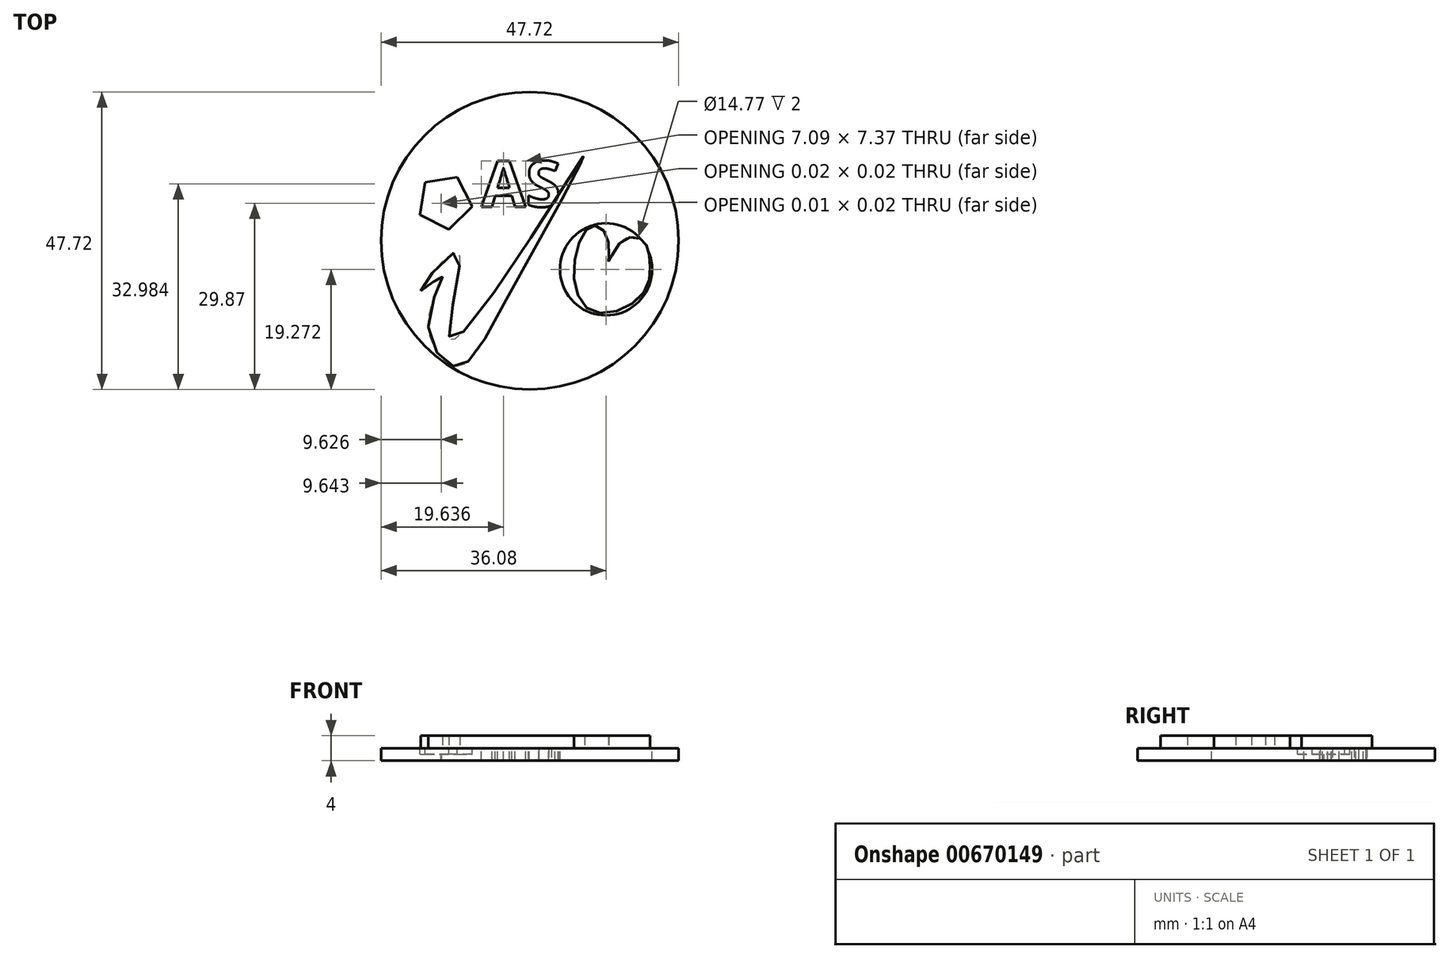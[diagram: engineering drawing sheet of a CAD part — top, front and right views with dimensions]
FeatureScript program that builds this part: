
annotation { "Feature Type Name" : "Feature", "Feature Type Description" : "" }
export const myFeature = defineFeature(function(context is Context, id is Id, definition is map)
    precondition{}
    {
        {
            var Q0;
            Q0=qCreatedBy(makeId("Top.planeOp"),FACE);
            var sketch = newSketch(context, id + "F0", { "sketchPlane" : qUnion([Q0])});
            skCircle(sketch, "E0", {"center": v(0, 0) * mm, "radius": 23.86 * mm});
            skSolve(sketch);
        }
        {
            var Q0;
            Q0=makeQuery(id+"F0.imprint","IMPRINT",FACE,{"disambiguationData":[TD([[makeQuery(id+"F0.imprint","IMPRINT",EDGE,{"derivedFrom":sQuery(id+"F0.wireOp",EDGE,"E0")}),1.0]])]});
            extrude(context, id + "F1", {"entities" : qUnion([Q0]), "oppositeDirection" : true, "depth" : 2 * mm, "offsetDistance" : 25.4 * mm});
        }
        {
            var Q0;
            Q0=makeQuery(id+"F0.imprint","IMPRINT",FACE,{"disambiguationData":[TD([[makeQuery(id+"F0.imprint","IMPRINT",EDGE,{"derivedFrom":sQuery(id+"F0.wireOp",EDGE,"E0")}),1.0]])]});
            var sketch = newSketch(context, id + "F2", { "sketchPlane" : qUnion([Q0])});
            skCircle(sketch, "E1.cCircle", {"center": v(-13.65, 6.19) * mm, "radius": 3.6 * mm, "construction": true});
            skLineSegment(sketch, "E1.0", {"start": v(-9.25, 5.5) * mm, "end": v(-12.96, 1.79) * mm});
            skLineSegment(sketch, "E1.1", {"start": v(-12.96, 1.79) * mm, "end": v(-17.62, 4.17) * mm});
            skLineSegment(sketch, "E1.2", {"start": v(-17.62, 4.17) * mm, "end": v(-16.8, 9.34) * mm});
            skLineSegment(sketch, "E1.3", {"start": v(-16.8, 9.34) * mm, "end": v(-11.63, 10.16) * mm});
            skLineSegment(sketch, "E1.4", {"start": v(-11.63, 10.16) * mm, "end": v(-9.25, 5.5) * mm});
            skPoint(sketch, "E1.0.midPoint", {"position": v(-11.1, 3.64) * mm});
            skSolve(sketch);
        }
        {
            var Q0;
            Q0 = qSketchRegion(id + "F2", true);
            extrude(context, id + "F3", {"entities" : qUnion([Q0]), "operationType" : NewBodyOperationType.REMOVE, "oppositeDirection" : true, "depth" : 1 * mm, "offsetDistance" : 25.4 * mm});
        }
        {
            var Q0;
            Q0=makeQuery(id+"F0.imprint","IMPRINT",FACE,{"disambiguationData":[TD([[makeQuery(id+"F0.imprint","IMPRINT",EDGE,{"derivedFrom":sQuery(id+"F0.wireOp",EDGE,"E0")}),1.0]])]});
            var sketch = newSketch(context, id + "F4", { "sketchPlane" : qUnion([Q0])});
            skCircle(sketch, "E2", {"center": v(12.22, -4.59) * mm, "radius": 7.38 * mm});
            skSolve(sketch);
        }
        {
            var Q0;
            Q0 = qSketchRegion(id + "F4", true);
            extrude(context, id + "F5", {"entities" : qUnion([Q0]), "operationType" : NewBodyOperationType.REMOVE, "oppositeDirection" : true, "depth" : 2 * mm, "offsetDistance" : 25.4 * mm});
        }
        {
            var Q0;
            Q0=makeQuery(id+"F0.imprint","IMPRINT",FACE,{"disambiguationData":[TD([[makeQuery(id+"F0.imprint","IMPRINT",EDGE,{"derivedFrom":sQuery(id+"F0.wireOp",EDGE,"E0")}),1.0]])]});
            var sketch = newSketch(context, id + "F6", { "sketchPlane" : qUnion([Q0])});
            skText(sketch, "E3", { "text": "AS", "fontName": "OpenSans-Italic.ttf"});
            skText(sketch, "E4", { "text": "AS", "fontName": "OpenSans-Bold.ttf"});
            const initialGuessF6  = {"E3": [-0.01424, 0.006, 1, 0, 2e-05], "E4": [-0.00777, 0.00544, 1, 0, 0.0074]};
            skSetInitialGuess(sketch, initialGuessF6);
            skSolve(sketch);
        }
        {
            var Q0;
            Q0 = qSketchRegion(id + "F6", true);
            extrude(context, id + "F7", {"entities" : qUnion([Q0]), "operationType" : NewBodyOperationType.REMOVE, "oppositeDirection" : true, "depth" : 2 * mm, "offsetDistance" : 25.4 * mm});
        }
        {
            var Q0;
            Q0=makeQuery(id+"F0.imprint","IMPRINT",FACE,{"disambiguationData":[TD([[makeQuery(id+"F0.imprint","IMPRINT",EDGE,{"derivedFrom":sQuery(id+"F0.wireOp",EDGE,"E0")}),1.0]])]});
            var sketch = newSketch(context, id + "F8", { "sketchPlane" : qUnion([Q0])});
            skFitSpline(sketch, "E5", {"points": [v(-17.5, -8.06) * mm, v(-11.6, -1.9) * mm, v(-12.67, -15.83) * mm, v(8.6, 13.53) * mm, v(-4.47, -10.75) * mm, v(-12.14, -20.14) * mm, v(-16.26, -12.66) * mm, v(-14.15, -5.62) * mm, v(-17.5, -8.06) * mm]});
            skSolve(sketch);
        }
        {
            var Q0;
            Q0 = qSketchRegion(id + "F8", true);
            extrude(context, id + "F9", {"entities" : qUnion([Q0]), "operationType" : NewBodyOperationType.ADD, "depth" : 2 * mm, "offsetDistance" : 25.4 * mm});
        }
        {
            var Q0;
            Q0=makeQuery(id+"F0.imprint","IMPRINT",FACE,{"disambiguationData":[TD([[makeQuery(id+"F0.imprint","IMPRINT",EDGE,{"derivedFrom":sQuery(id+"F0.wireOp",EDGE,"E0")}),1.0]])]});
            var sketch = newSketch(context, id + "F10", { "sketchPlane" : qUnion([Q0])});
            skPoint(sketch, "E6.0.internal.orphan", {"position": v(0, 21.3) * mm});
            skFitSpline(sketch, "E7", {"points": [v(12.63, -3.34) * mm, v(12.57, 0) * mm, v(10.17, 2.42) * mm, v(7.11, -3.72) * mm, v(10.1, -11.33) * mm, v(18, -8.67) * mm, v(19.22, -3.23) * mm, v(18.14, 0) * mm, v(14.84, 0) * mm, v(12.63, -3.34) * mm]});
            skSolve(sketch);
        }
        {
            var Q0;
            Q0 = qSketchRegion(id + "F10", true);
            extrude(context, id + "F11", {"entities" : qUnion([Q0]), "operationType" : NewBodyOperationType.ADD, "depth" : 2 * mm, "offsetDistance" : 25.4 * mm});
        }
    });
